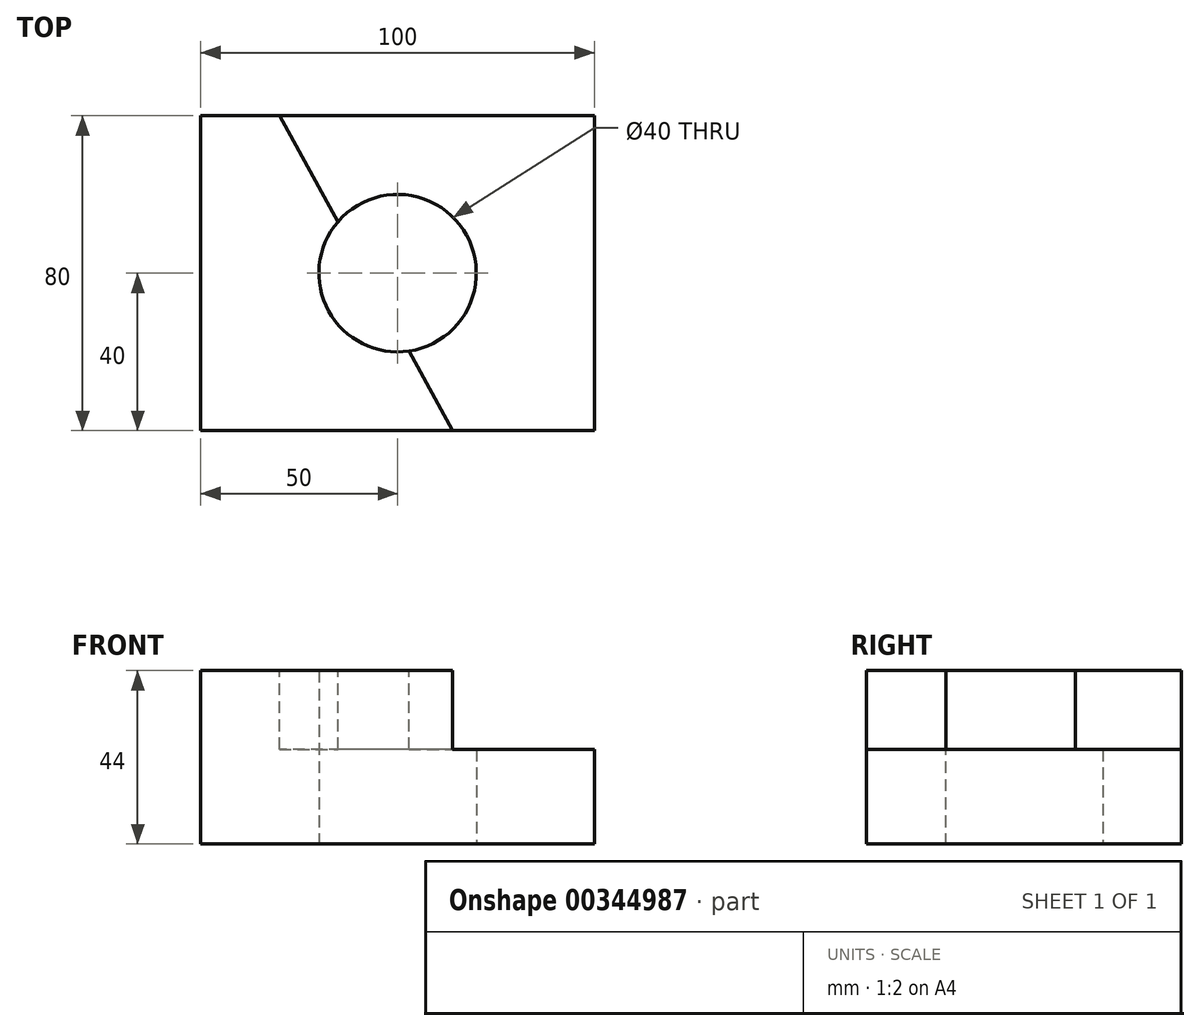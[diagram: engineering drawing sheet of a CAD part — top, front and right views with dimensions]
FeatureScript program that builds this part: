
annotation { "Feature Type Name" : "Feature", "Feature Type Description" : "" }
export const myFeature = defineFeature(function(context is Context, id is Id, definition is map)
    precondition{}
    {
        {
            var Q0;
            Q0=qCreatedBy(makeId("Top.planeOp"),FACE);
            var sketch = newSketch(context, id + "F0", { "sketchPlane" : qUnion([Q0])});
            skLineSegment(sketch, "E0.bottom", {"start": v(50, -40) * mm, "end": v(-50, -40) * mm});
            skLineSegment(sketch, "E0.top", {"start": v(50, 40) * mm, "end": v(-50, 40) * mm});
            skLineSegment(sketch, "E0.left", {"start": v(50, -40) * mm, "end": v(50, 40) * mm});
            skLineSegment(sketch, "E0.right", {"start": v(-50, -40) * mm, "end": v(-50, 40) * mm});
            skPoint(sketch, "E0.middle", {"position": v(0, 0) * mm});
            skCircle(sketch, "E1", {"center": v(0, 0) * mm, "radius": 20 * mm});
            skLineSegment(sketch, "E2", {"start": v(-50, 40) * mm, "end": v(-14, 40) * mm, "construction": true});
            skLineSegment(sketch, "E3", {"start": v(-50, -40) * mm, "end": v(30, -40) * mm, "construction": true});
            skSolve(sketch);
        }
        {
            var Q0;
            Q0=makeQuery(id+"F0.imprint","IMPRINT",FACE,{"disambiguationData":[TD([[makeQuery(id+"F0.imprint","IMPRINT",EDGE,{"derivedFrom":sQuery(id+"F0.wireOp",EDGE,"E0.bottom")}),-1.0]])]});
            extrude(context, id + "F1", {"entities" : qUnion([Q0]), "depth" : 44 * mm});
        }
        {
            var Q0;
            Q0=makeQuery(id+"F1.opExtrude","CAP_FACE",FACE,{"disambiguationData":[OSD([sQuery(id+"F0.wireOp",EDGE,"E0.bottom"),sQuery(id+"F0.wireOp",EDGE,"E0.top"),sQuery(id+"F0.wireOp",EDGE,"E0.left"),sQuery(id+"F0.wireOp",EDGE,"E0.right"),sQuery(id+"F0.wireOp",EDGE,"E1")])],"isStart":false});
            var sketch = newSketch(context, id + "F2", { "sketchPlane" : qUnion([Q0])});
            skLineSegment(sketch, "E4", {"start": v(50, 40) * mm, "end": v(-30, 40) * mm});
            skLineSegment(sketch, "E5", {"start": v(50, -40) * mm, "end": v(14, -40) * mm});
            skLineSegment(sketch, "E6", {"start": v(-30, 40) * mm, "end": v(14, -40) * mm});
            skSolve(sketch);
        }
        {
            var Q0;
            Q0 = qSketchRegion(id + "F2", true);
            var Q1;
            {var subQ4=sQuery(id+"F2.wireOp",EDGE,"E4");Q1=makeQuery(id+"F2.imprint","IMPRINT",FACE,{"disambiguationData":[TD([[makeQuery(id+"F2.imprint","IMPRINT",EDGE,{"derivedFrom":subQ4}),1.0]])]});}
            extrude(context, id + "F3", {"entities" : qUnion([Q0, Q1]), "operationType" : NewBodyOperationType.REMOVE, "oppositeDirection" : true, "depth" : 20 * mm});
        }
    });
